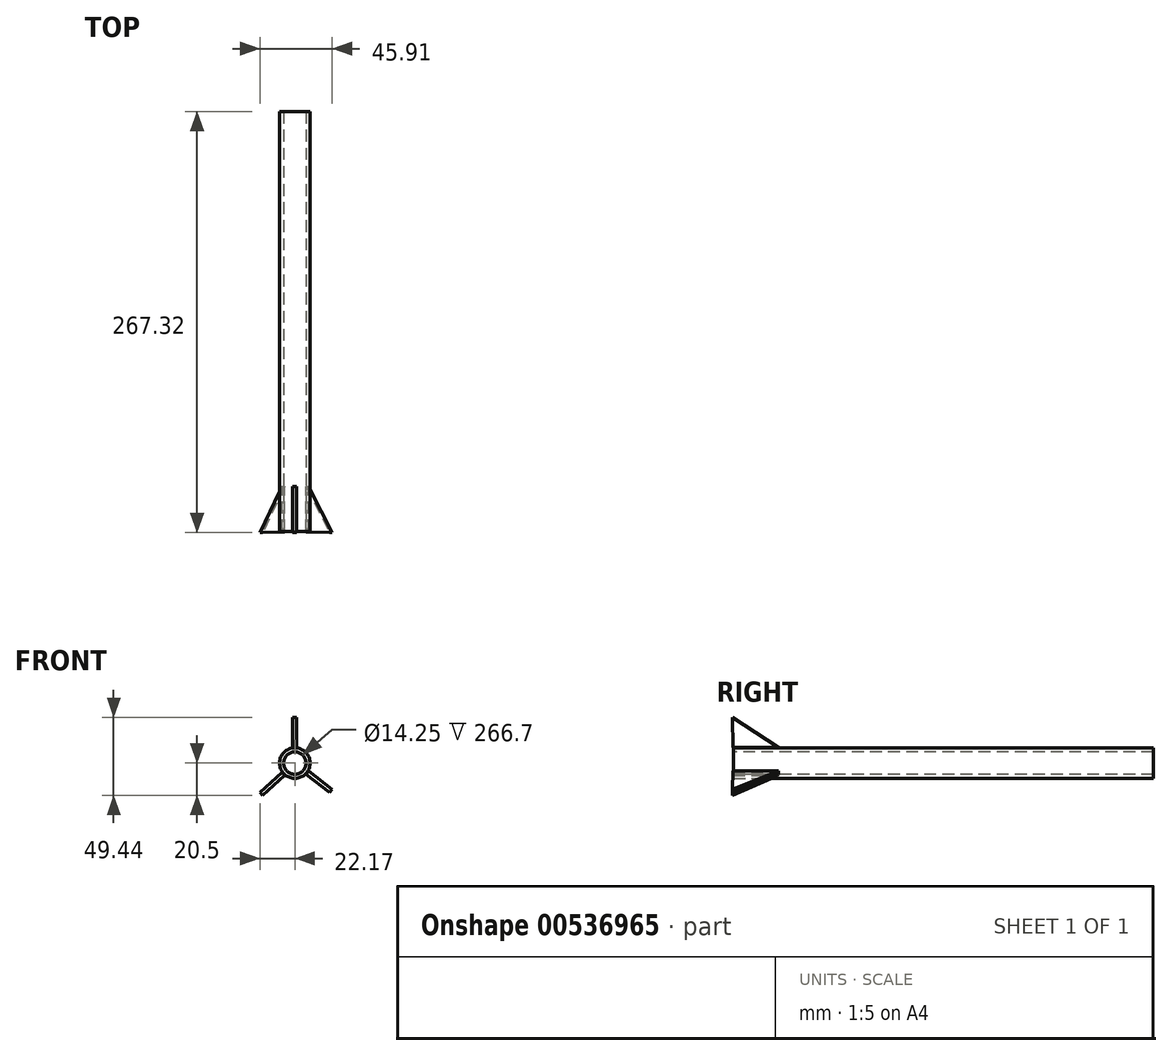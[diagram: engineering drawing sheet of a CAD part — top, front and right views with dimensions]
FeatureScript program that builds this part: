
annotation { "Feature Type Name" : "Feature", "Feature Type Description" : "" }
export const myFeature = defineFeature(function(context is Context, id is Id, definition is map)
    precondition{}
    {
        {
            var Q0;
            Q0=qCreatedBy(makeId("Front.planeOp"),FACE);
            var sketch = newSketch(context, id + "F0", { "sketchPlane" : qUnion([Q0])});
            skCircle(sketch, "E0", {"center": v(0, 0) * mm, "radius": 9.53 * mm});
            skCircle(sketch, "E1", {"center": v(0, 0) * mm, "radius": 9.67 * mm});
            skSolve(sketch);
        }
        {
            var Q0;
            Q0 = qSketchRegion(id + "F0", true);
            var Q1;
            Q1=makeQuery(id+"F0.imprint","IMPRINT",FACE,{"disambiguationData":[TD([[makeQuery(id+"F0.imprint","IMPRINT",EDGE,{"derivedFrom":sQuery(id+"F0.wireOp",EDGE,"E0")}),1.0]])]});
            extrude(context, id + "F1", {"entities" : qUnion([Q0, Q1]), "endBound" : BoundingType.SYMMETRIC, "depth" : 266.7 * mm, "offsetDistance" : 25.4 * mm});
        }
        {
            var Q0;
            Q0=qCreatedBy(makeId("Front.planeOp"),FACE);
            var sketch = newSketch(context, id + "F2", { "sketchPlane" : qUnion([Q0])});
            skCircle(sketch, "E2", {"center": v(0, 0) * mm, "radius": 7.13 * mm});
            skSolve(sketch);
        }
        {
            var Q0;
            Q0 = qSketchRegion(id + "F2", true);
            extrude(context, id + "F3", {"entities" : qUnion([Q0]), "operationType" : NewBodyOperationType.REMOVE, "endBound" : BoundingType.SYMMETRIC, "oppositeDirection" : true, "depth" : 266.7 * mm, "offsetDistance" : 25.4 * mm});
        }
        {
            var Q0;
            Q0=qCreatedBy(makeId("Right.planeOp"),FACE);
            var sketch = newSketch(context, id + "F4", { "sketchPlane" : qUnion([Q0])});
            skLineSegment(sketch, "E3", {"start": v(-133.56, 9.99) * mm, "end": v(-104.72, 9.99) * mm});
            skLineSegment(sketch, "E4", {"start": v(-104.72, 9.99) * mm, "end": v(-133.97, 28.94) * mm});
            skLineSegment(sketch, "E5", {"start": v(-133.97, 28.94) * mm, "end": v(-133.56, 9.99) * mm});
            skSolve(sketch);
        }
        {
            var Q0;
            Q0 = qSketchRegion(id + "F4", true);
            extrude(context, id + "F5", {"entities" : qUnion([Q0]), "endBound" : BoundingType.SYMMETRIC, "depth" : 2.54 * mm, "offsetDistance" : 25.4 * mm});
        }
        {
            var Q0;
            Q0=makeQuery(id+"F5.opExtrude","SWEPT_BODY",BODY,{"disambiguationData":[OSD([sQuery(id+"F4.wireOp",EDGE,"E3"),sQuery(id+"F4.wireOp",EDGE,"E4"),sQuery(id+"F4.wireOp",EDGE,"E5")])]});
            var Q1;
            Q1=makeQuery(id+"F1.opExtrude","CAP_EDGE",EDGE,{"disambiguationData":[OSD([sQuery(id+"F0.wireOp",EDGE,"E1")])],"isStart":false});
            transform(context, id + "F6", {"entities" : qUnion([Q0]), "transformType" : TransformType.ROTATION, "transformAxis" : qUnion([Q1]), "angle" : 132.55 * degree, "makeCopy" : true});
        }
        {
            var Q0;
            Q0=makeQuery(id+"F6.opPattern","COPY",BODY,{"derivedFrom":makeQuery(id+"F5.opExtrude","SWEPT_BODY",BODY,{"disambiguationData":[OSD([sQuery(id+"F4.wireOp",EDGE,"E3"),sQuery(id+"F4.wireOp",EDGE,"E4"),sQuery(id+"F4.wireOp",EDGE,"E5")])]}),"instanceName":"1"});
            var Q1;
            Q1=makeQuery(id+"F1.opExtrude","CAP_EDGE",EDGE,{"disambiguationData":[OSD([sQuery(id+"F0.wireOp",EDGE,"E1")])],"isStart":false});
            transform(context, id + "F7", {"entities" : qUnion([Q0]), "transformType" : TransformType.ROTATION, "transformAxis" : qUnion([Q1]), "angle" : 100 * degree, "makeCopy" : true});
        }
    });
